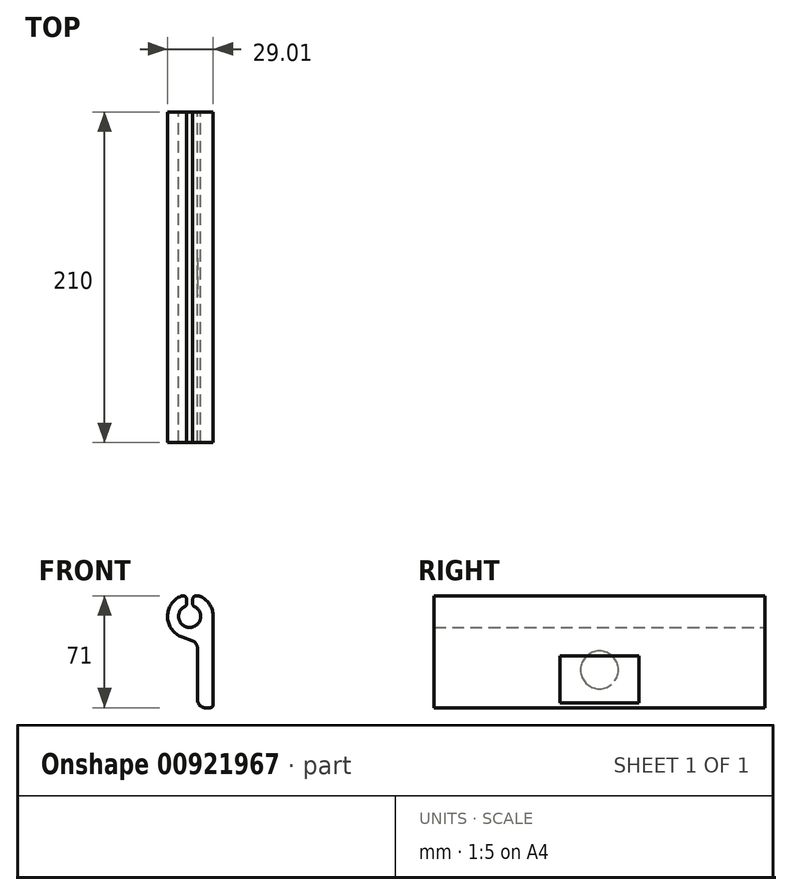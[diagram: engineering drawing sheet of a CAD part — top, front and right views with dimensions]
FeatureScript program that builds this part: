
annotation { "Feature Type Name" : "Feature", "Feature Type Description" : "" }
export const myFeature = defineFeature(function(context is Context, id is Id, definition is map)
    precondition{}
    {
        {
            var Q0;
            Q0=qCreatedBy(makeId("Front.planeOp"),FACE);
            var sketch = newSketch(context, id + "F0", { "sketchPlane" : qUnion([Q0])});
            skArc(sketch, "E0", {"start": v(4.5, -30.5) * mm, "mid": v(5.96, -34.04) * mm, "end": v(9.5, -35.5) * mm});
            skLineSegment(sketch, "E1", {"start": v(9.5, -35.5) * mm, "end": v(12.5, -35.5) * mm});
            skArc(sketch, "E2", {"start": v(12.5, -35.5) * mm, "mid": v(13.91, -34.91) * mm, "end": v(14.5, -33.5) * mm});
            skLineSegment(sketch, "E3", {"start": v(14.5, -33.5) * mm, "end": v(14.5, 22.5) * mm});
            skArc(sketch, "E4", {"start": v(14.5, 22.5) * mm, "mid": v(12.45, 29.79) * mm, "end": v(6.91, 34.94) * mm});
            skArc(sketch, "E5", {"start": v(6.91, 34.94) * mm, "mid": v(5.8, 35.36) * mm, "end": v(4.62, 35.5) * mm});
            skLineSegment(sketch, "E6", {"start": v(4.62, 35.5) * mm, "end": v(3.5, 35.5) * mm});
            skArc(sketch, "E7", {"start": v(3.5, 35.5) * mm, "mid": v(2.09, 34.91) * mm, "end": v(1.5, 33.5) * mm});
            skLineSegment(sketch, "E8", {"start": v(1.5, 33.5) * mm, "end": v(1.5, 30.25) * mm});
            skArc(sketch, "E9", {"start": v(1.5, 30.25) * mm, "mid": v(1.74, 29.43) * mm, "end": v(2.38, 28.88) * mm});
            skArc(sketch, "E10", {"start": v(-3.38, 28.88) * mm, "mid": v(-0.5, 15.5) * mm, "end": v(2.38, 28.88) * mm});
            skArc(sketch, "E11", {"start": v(-3.38, 28.88) * mm, "mid": v(-2.74, 29.43) * mm, "end": v(-2.5, 30.25) * mm});
            skLineSegment(sketch, "E12", {"start": v(-2.5, 30.25) * mm, "end": v(-2.5, 33.5) * mm});
            skArc(sketch, "E13", {"start": v(-2.5, 33.5) * mm, "mid": v(-3.09, 34.91) * mm, "end": v(-4.5, 35.5) * mm});
            skLineSegment(sketch, "E14", {"start": v(-4.5, 35.5) * mm, "end": v(-4.62, 35.5) * mm});
            skArc(sketch, "E15", {"start": v(-4.62, 35.5) * mm, "mid": v(-5.8, 35.36) * mm, "end": v(-6.91, 34.94) * mm});
            skArc(sketch, "E16", {"start": v(-6.91, 34.94) * mm, "mid": v(-14.47, 21.61) * mm, "end": v(-5.29, 9.34) * mm});
            skLineSegment(sketch, "E17", {"start": v(-5.29, 9.34) * mm, "end": v(1.21, 6.98) * mm});
            skArc(sketch, "E18", {"start": v(4.5, 2.28) * mm, "mid": v(3.6, 5.15) * mm, "end": v(1.21, 6.98) * mm});
            skLineSegment(sketch, "E19", {"start": v(4.5, 2.28) * mm, "end": v(4.5, -30.5) * mm});
            skLineSegment(sketch, "E20", {"start": v(4.5, -23.5) * mm, "end": v(4.4, -23.5) * mm});
            skLineSegment(sketch, "E21", {"start": v(4.4, -23.5) * mm, "end": v(4.4, 0.5) * mm});
            skLineSegment(sketch, "E22", {"start": v(4.4, 0.5) * mm, "end": v(4.5, 0.5) * mm});
            skSolve(sketch);
        }
        {
            var Q0;
            {var subQ0=sQuery(id+"F0.wireOp",EDGE,"E0");Q0=makeQuery(id+"F0.imprint","IMPRINT",FACE,{"disambiguationData":[TD([[makeQuery(id+"F0.imprint","IMPRINT",EDGE,{"derivedFrom":subQ0}),1.0]])]});}
            extrude(context, id + "F1", {"entities" : qUnion([Q0]), "endBound" : BoundingType.SYMMETRIC, "depth" : 210 * mm, "offsetDistance" : 25 * mm});
        }
        {
            var Q0;
            Q0=makeQuery(id+"F1.opExtrude","SWEPT_FACE",FACE,{"disambiguationData":[OSD([sQuery(id+"F0.wireOp",EDGE,"E19")])]});
            var sketch = newSketch(context, id + "F2", { "sketchPlane" : qUnion([Q0])});
            skCircle(sketch, "E23", {"center": v(0, -11.5) * mm, "radius": 12 * mm});
            skSolve(sketch);
        }
        {
            var Q0;
            Q0=makeQuery(id+"F2.imprint","IMPRINT",FACE,{"disambiguationData":[TD([[makeQuery(id+"F2.imprint","IMPRINT",EDGE,{"derivedFrom":sQuery(id+"F2.wireOp",EDGE,"E23")}),1.0]])]});
            extrude(context, id + "F3", {"entities" : qUnion([Q0]), "operationType" : NewBodyOperationType.ADD, "depth" : 0.05 * mm, "offsetDistance" : 25 * mm});
        }
        {
            var Q0;
            Q0=makeQuery(id+"F1.opExtrude","SWEPT_FACE",FACE,{"disambiguationData":[OSD([sQuery(id+"F0.wireOp",EDGE,"E3")])]});
            var sketch = newSketch(context, id + "F4", { "sketchPlane" : qUnion([Q0])});
            skLineSegment(sketch, "E24.bottom", {"start": v(25, -2.5) * mm, "end": v(-25, -2.5) * mm});
            skLineSegment(sketch, "E24.top", {"start": v(25, -32.5) * mm, "end": v(-25, -32.5) * mm});
            skLineSegment(sketch, "E24.left", {"start": v(25, -2.5) * mm, "end": v(25, -32.5) * mm});
            skLineSegment(sketch, "E24.right", {"start": v(-25, -2.5) * mm, "end": v(-25, -32.5) * mm});
            skPoint(sketch, "E24.middle", {"position": v(0, -17.5) * mm});
            skPoint(sketch, "E24.middle.positionSnap0", {"position": v(0, -33.5) * mm});
            skPoint(sketch, "E24.centerSnap0", {"position": v(0, -33.5) * mm});
            skSolve(sketch);
        }
        {
            var Q0;
            Q0=makeQuery(id+"F4.imprint","IMPRINT",FACE,{"disambiguationData":[TD([[makeQuery(id+"F4.imprint","IMPRINT",EDGE,{"derivedFrom":sQuery(id+"F4.wireOp",EDGE,"E24.bottom")}),1.0]])]});
            extrude(context, id + "F5", {"entities" : qUnion([Q0]), "operationType" : NewBodyOperationType.ADD, "depth" : 0.01 * mm, "offsetDistance" : 25 * mm});
        }
    });
